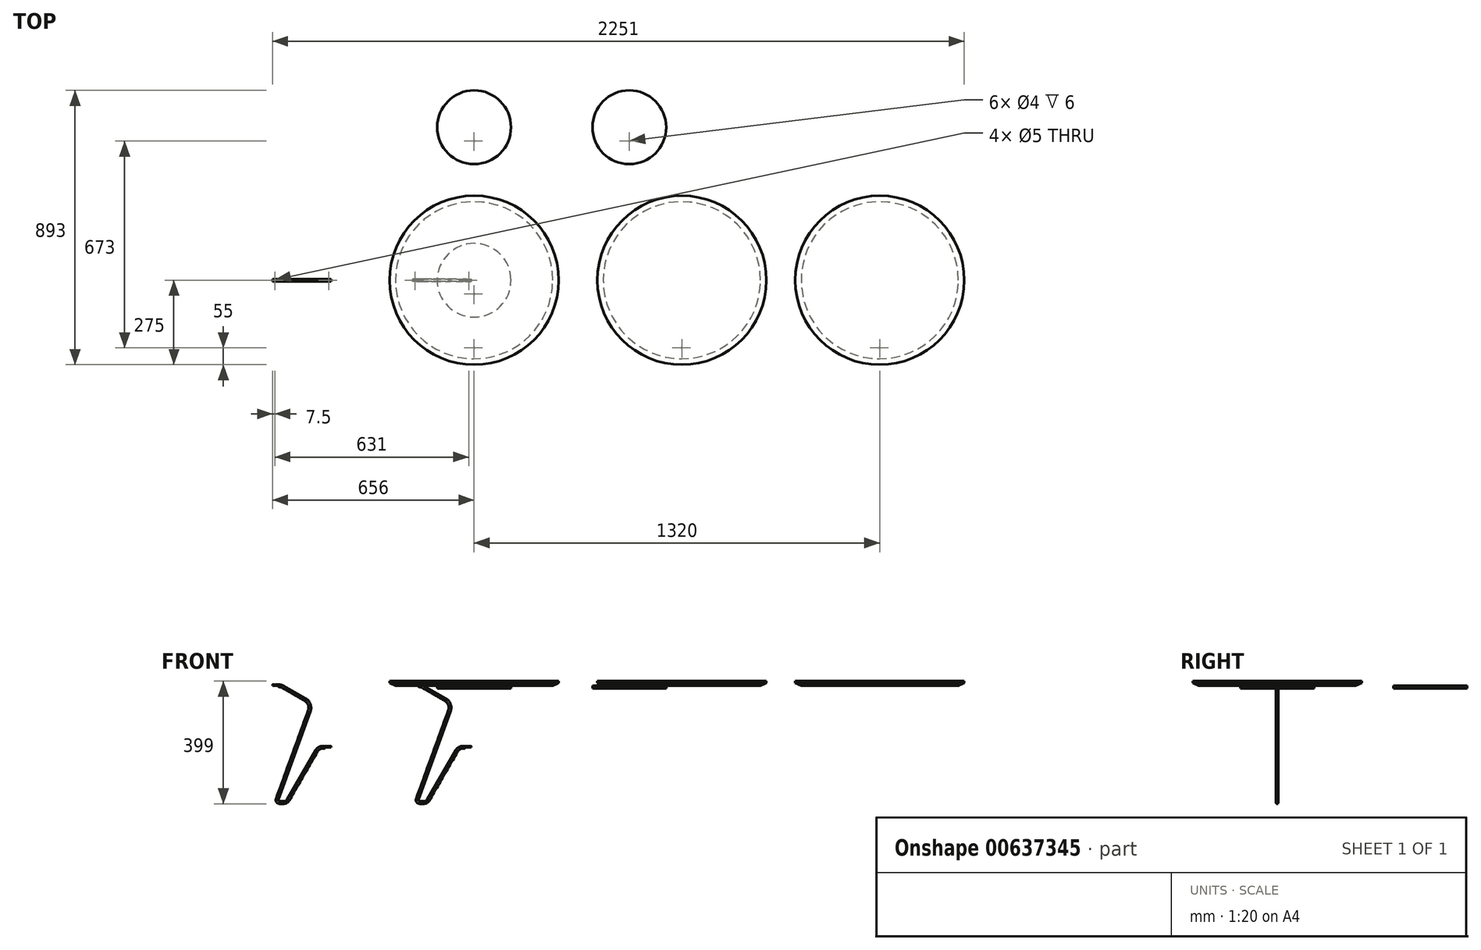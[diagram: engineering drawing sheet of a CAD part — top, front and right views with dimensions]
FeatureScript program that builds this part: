
annotation { "Feature Type Name" : "Feature", "Feature Type Description" : "" }
export const myFeature = defineFeature(function(context is Context, id is Id, definition is map)
    precondition{}
    {
        {
            var Q0;
            Q0=qCreatedBy(makeId("Front.planeOp"),FACE);
            var sketch = newSketch(context, id + "F0", { "sketchPlane" : qUnion([Q0])});
            skLineSegment(sketch, "E0", {"start": v(-200, 0) * mm, "end": v(-180, 0) * mm});
            skLineSegment(sketch, "E1", {"start": v(-165, -4.02) * mm, "end": v(-93.49, -45.3) * mm});
            skLineSegment(sketch, "E2", {"start": v(-80.3, -81.55) * mm, "end": v(-185.02, -369.26) * mm});
            skLineSegment(sketch, "E3", {"start": v(-177.5, -380) * mm, "end": v(-163.16, -380) * mm});
            skLineSegment(sketch, "E4", {"start": v(-149.3, -372) * mm, "end": v(-57.22, -212.5) * mm});
            skLineSegment(sketch, "E5", {"start": v(-35.57, -200) * mm, "end": v(0, -200) * mm});
            skPoint(sketch, "E6.visualSharp", {"position": v(-71.69, -57.9) * mm});
            skArc(sketch, "E6.filletArc", {"start": v(-80.3, -81.55) * mm, "mid": v(-80.3, -61.03) * mm, "end": v(-93.49, -45.3) * mm});
            skPoint(sketch, "E7.visualSharp", {"position": v(-50, -200) * mm});
            skArc(sketch, "E7.filletArc", {"start": v(-35.57, -200) * mm, "mid": v(-48.07, -203.35) * mm, "end": v(-57.22, -212.5) * mm});
            skPoint(sketch, "E8.visualSharp", {"position": v(-153.92, -380) * mm});
            skArc(sketch, "E8.filletArc", {"start": v(-163.16, -380) * mm, "mid": v(-155.16, -377.86) * mm, "end": v(-149.3, -372) * mm});
            skPoint(sketch, "E9.visualSharp", {"position": v(-188.92, -380) * mm});
            skArc(sketch, "E9.filletArc", {"start": v(-185.02, -369.26) * mm, "mid": v(-184.05, -376.59) * mm, "end": v(-177.5, -380) * mm});
            skPoint(sketch, "E10.visualSharp", {"position": v(-171.96, 0) * mm});
            skArc(sketch, "E10.filletArc", {"start": v(-165, -4.02) * mm, "mid": v(-172.24, -1.02) * mm, "end": v(-180, 0) * mm});
            skSolve(sketch);
        }
        {
            var Q0;
            Q0=qCreatedBy(makeId("Right.planeOp"),FACE);
            var sketch = newSketch(context, id + "F1", { "sketchPlane" : qUnion([Q0])});
            skCircle(sketch, "E11", {"center": v(0, -200) * mm, "radius": 4 * mm});
            skSolve(sketch);
        }
        {
            var Q0;
            Q0=makeQuery(id+"F1.imprint","IMPRINT",FACE,{"disambiguationData":[TD([[makeQuery(id+"F1.imprint","IMPRINT",EDGE,{"derivedFrom":sQuery(id+"F1.wireOp",EDGE,"E11")}),1.0]])]});
            var Q1;
            Q1=sQuery(id+"F0.wireOp",EDGE,"E5");
            var Q2;
            Q2=sQuery(id+"F0.wireOp",EDGE,"E7.filletArc");
            var Q3;
            Q3=sQuery(id+"F0.wireOp",EDGE,"E4");
            var Q4;
            Q4=sQuery(id+"F0.wireOp",EDGE,"E8.filletArc");
            var Q5;
            Q5=sQuery(id+"F0.wireOp",EDGE,"E3");
            var Q6;
            Q6=sQuery(id+"F0.wireOp",EDGE,"E9.filletArc");
            var Q7;
            Q7=sQuery(id+"F0.wireOp",EDGE,"E2");
            var Q8;
            Q8=sQuery(id+"F0.wireOp",EDGE,"E6.filletArc");
            var Q9;
            Q9=sQuery(id+"F0.wireOp",EDGE,"E1");
            var Q10;
            Q10=sQuery(id+"F0.wireOp",EDGE,"E10.filletArc");
            var Q11;
            Q11=sQuery(id+"F0.wireOp",EDGE,"E0");
            sweep(context, id + "F2", {"profiles" : qUnion([Q0]), "path" : qUnion([Q1, Q2, Q3, Q4, Q5, Q6, Q7, Q8, Q9, Q10, Q11])});
        }
        {
            var Q0;
            Q0=makeQuery(id+"F2.opSweep","CAP_FACE",FACE,{"disambiguationData":[OSD([sQuery(id+"F0.wireOp",VERTEX,"E0.start"),sQuery(id+"F1.wireOp",EDGE,"E11")])],"isStart":false});
            var sketch = newSketch(context, id + "F3", { "sketchPlane" : qUnion([Q0])});
            skLineSegment(sketch, "E12", {"start": v(4, 0) * mm, "end": v(-4, 0) * mm});
            skArc(sketch, "E13", {"start": v(-4, 0) * mm, "mid": v(0, -4) * mm, "end": v(4, 0) * mm});
            skSolve(sketch);
        }
        {
            var Q0;
            Q0 = qSketchRegion(id + "F3", true);
            extrude(context, id + "F4", {"entities" : qUnion([Q0]), "operationType" : NewBodyOperationType.REMOVE, "oppositeDirection" : true, "depth" : 20 * mm, "offsetDistance" : 25 * mm});
        }
        {
            var Q0;
            Q0=makeQuery(id+"F4.boolean.opBoolean","COPY",FACE,{"derivedFrom":makeQuery(id+"F4.opExtrude","SWEPT_FACE",FACE,{"disambiguationData":[OSD([sQuery(id+"F3.wireOp",EDGE,"E12")])]})});
            var sketch = newSketch(context, id + "F5", { "sketchPlane" : qUnion([Q0])});
            skCircle(sketch, "E14", {"center": v(-192.5, 0) * mm, "radius": 2.5 * mm});
            skPoint(sketch, "E14.centerSnap0", {"position": v(-200, 0) * mm});
            skSolve(sketch);
        }
        {
            var Q0;
            Q0 = qSketchRegion(id + "F5", true);
            extrude(context, id + "F6", {"entities" : qUnion([Q0]), "operationType" : NewBodyOperationType.REMOVE, "endBound" : BoundingType.THROUGH_ALL, "oppositeDirection" : true, "depth" : 25 * mm, "offsetDistance" : 25 * mm});
        }
        {
            var Q0;
            Q0=makeQuery(id+"F2.opSweep","CAP_FACE",FACE,{"disambiguationData":[OSD([sQuery(id+"F0.wireOp",VERTEX,"E5.end"),sQuery(id+"F1.wireOp",EDGE,"E11")])],"isStart":true});
            extrude(context, id + "F7", {"entities" : qUnion([Q0]), "operationType" : NewBodyOperationType.REMOVE, "oppositeDirection" : true, "depth" : 10 * mm, "offsetDistance" : 25 * mm});
        }
        {
            var Q0;
            Q0=makeQuery(id+"F7.boolean.opBoolean","COPY",FACE,{"derivedFrom":makeQuery(id+"F7.opExtrude","CAP_FACE",FACE,{"disambiguationData":[OSD([sQuery(id+"F0.wireOp",VERTEX,"E5.end"),sQuery(id+"F1.wireOp",EDGE,"E11")])],"isStart":false})});
            var sketch = newSketch(context, id + "F8", { "sketchPlane" : qUnion([Q0])});
            skLineSegment(sketch, "E15", {"start": v(-4, -200) * mm, "end": v(4, -200) * mm});
            skPoint(sketch, "E16", {"position": v(0, -200) * mm});
            skArc(sketch, "E17", {"start": v(-4, -200) * mm, "mid": v(0, -204) * mm, "end": v(4, -200) * mm});
            skSolve(sketch);
        }
        {
            var Q0;
            Q0 = qSketchRegion(id + "F8", true);
            extrude(context, id + "F9", {"entities" : qUnion([Q0]), "operationType" : NewBodyOperationType.REMOVE, "oppositeDirection" : true, "depth" : 20 * mm, "offsetDistance" : 25 * mm});
        }
        {
            var Q0;
            Q0=makeQuery(id+"F9.boolean.opBoolean","COPY",FACE,{"derivedFrom":makeQuery(id+"F9.opExtrude","SWEPT_FACE",FACE,{"disambiguationData":[OSD([sQuery(id+"F8.wireOp",EDGE,"E15")])]})});
            var sketch = newSketch(context, id + "F10", { "sketchPlane" : qUnion([Q0])});
            skCircle(sketch, "E18", {"center": v(-17.5, 0) * mm, "radius": 2.5 * mm});
            skPoint(sketch, "E18.centerSnap0", {"position": v(-10, 0) * mm});
            skSolve(sketch);
        }
        {
            var Q0;
            Q0 = qSketchRegion(id + "F10", true);
            extrude(context, id + "F11", {"entities" : qUnion([Q0]), "operationType" : NewBodyOperationType.REMOVE, "endBound" : BoundingType.THROUGH_ALL, "oppositeDirection" : true, "depth" : 25 * mm, "offsetDistance" : 25 * mm});
        }
        {
            var Q0;
            Q0=makeQuery(id+"F4.boolean.opBoolean","COPY",EDGE,{"derivedFrom":makeQuery(id+"F4.opExtrude","CAP_EDGE",EDGE,{"disambiguationData":[OSD([sQuery(id+"F3.wireOp",EDGE,"E12")])],"isStart":false})});
            var Q1;
            Q1=makeQuery(id+"F9.boolean.opBoolean","COPY",EDGE,{"derivedFrom":makeQuery(id+"F9.opExtrude","CAP_EDGE",EDGE,{"disambiguationData":[OSD([sQuery(id+"F8.wireOp",EDGE,"E15")])],"isStart":false})});
            fillet(context, id + "F12", {"entities" : qUnion([Q0, Q1]), "radius" : 5 * mm, "tangentPropagation" : true, "allowEdgeOverflow" : false});
        }
        {
            var Q0;
            Q0=qCreatedBy(makeId("Top.planeOp"),FACE);
            var sketch = newSketch(context, id + "F13", { "sketchPlane" : qUnion([Q0])});
            skCircle(sketch, "E19", {"center": v(0, 0) * mm, "radius": 275 * mm});
            skSolve(sketch);
        }
        {
            var Q0;
            Q0 = qSketchRegion(id + "F13", true);
            extrude(context, id + "F14", {"entities" : qUnion([Q0]), "depth" : 15 * mm, "offsetDistance" : 25 * mm});
        }
        {
            var Q0;
            Q0=qCreatedBy(makeId("Top.planeOp"),FACE);
            var sketch = newSketch(context, id + "F15", { "sketchPlane" : qUnion([Q0])});
            skCircle(sketch, "E20", {"center": v(0, 0) * mm, "radius": 120 * mm});
            skSolve(sketch);
        }
        {
            var Q0;
            Q0=makeQuery(id+"F15.imprint","IMPRINT",FACE,{"disambiguationData":[TD([[makeQuery(id+"F15.imprint","IMPRINT",EDGE,{"derivedFrom":sQuery(id+"F15.wireOp",EDGE,"E20")}),1.0]])]});
            var Q1;
            Q1=sQuery(id+"F15.wireOp",EDGE,"E20");
            extrude(context, id + "F16", {"entities" : qUnion([Q0]), "surfaceEntities" : qUnion([Q1]), "oppositeDirection" : true, "depth" : 9 * mm, "offsetDistance" : 25 * mm});
        }
        {
            var Q0;
            Q0=makeQuery(id+"F14.opExtrude","CAP_EDGE",EDGE,{"disambiguationData":[OSD([sQuery(id+"F13.wireOp",EDGE,"E19")])],"isStart":true});
            chamfer(context, id + "F17", {"entities" : qUnion([Q0]), "chamferType" : ChamferType.OFFSET_ANGLE, "width" : 9 * mm, "oppositeDirection" : false, "angle" : 65 * degree, "tangentPropagation" : true});
        }
        {
            var Q0;
            Q0=qCreatedBy(makeId("Front.planeOp"),FACE);
            var sketch = newSketch(context, id + "F18", { "sketchPlane" : qUnion([Q0])});
            skLineSegment(sketch, "E21", {"start": v(0, 0) * mm, "end": v(0, -50) * mm, "construction": true});
            skSolve(sketch);
        }
        {
            var Q0;
            Q0=makeQuery(id+"F16.opExtrude","CAP_FACE",FACE,{"disambiguationData":[OSD([sQuery(id+"F15.wireOp",EDGE,"E20")])],"isStart":false});
            var sketch = newSketch(context, id + "F19", { "sketchPlane" : qUnion([Q0])});
            skCircle(sketch, "E22", {"center": v(0, 45) * mm, "radius": 2 * mm});
            skCircle(sketch, "E23", {"center": v(0, 0) * mm, "radius": 45 * mm, "construction": true});
            skSolve(sketch);
        }
        {
            var Q0;
            Q0=makeQuery(id+"F19.imprint","IMPRINT",FACE,{"disambiguationData":[TD([[makeQuery(id+"F19.imprint","IMPRINT",EDGE,{"derivedFrom":sQuery(id+"F19.wireOp",EDGE,"E22")}),1.0]])]});
            var Q1;
            Q1=sQuery(id+"F19.wireOp",EDGE,"E22");
            extrude(context, id + "F20", {"entities" : qUnion([Q0]), "operationType" : NewBodyOperationType.REMOVE, "surfaceEntities" : qUnion([Q1]), "oppositeDirection" : true, "depth" : 6 * mm, "offsetDistance" : 25 * mm});
        }
        {
            var Q0;
            Q0=makeQuery(id+"F14.opExtrude","CAP_FACE",FACE,{"disambiguationData":[OSD([sQuery(id+"F13.wireOp",EDGE,"E19")])],"isStart":true});
            var sketch = newSketch(context, id + "F21", { "sketchPlane" : qUnion([Q0])});
            skCircle(sketch, "E24", {"center": v(0, 0) * mm, "radius": 220 * mm, "construction": true});
            skCircle(sketch, "E25", {"center": v(0, 220) * mm, "radius": 2 * mm});
            skSolve(sketch);
        }
        {
            var Q0;
            Q0 = qSketchRegion(id + "F21", true);
            extrude(context, id + "F22", {"entities" : qUnion([Q0]), "operationType" : NewBodyOperationType.REMOVE, "oppositeDirection" : true, "depth" : 6 * mm, "offsetDistance" : 25 * mm});
        }
        {
            var Q0;
            Q0=makeQuery(id+"F16.opExtrude","SWEPT_BODY",BODY,{"disambiguationData":[OSD([sQuery(id+"F15.wireOp",EDGE,"E20")])]});
            transform(context, id + "F23", {"entities" : qUnion([Q0]), "transformType" : TransformType.TRANSLATION_3D, "dx" : 0 * mm, "dy" : 498 * mm, "dz" : 0 * mm, "makeCopy" : true});
        }
        {
            var Q0;
            Q0=makeQuery(id+"F14.opExtrude","SWEPT_BODY",BODY,{"disambiguationData":[OSD([sQuery(id+"F13.wireOp",EDGE,"E19")])]});
            transform(context, id + "F24", {"entities" : qUnion([Q0]), "transformType" : TransformType.TRANSLATION_3D, "dx" : 1320 * mm, "dy" : 0 * mm, "dz" : 0 * mm, "makeCopy" : true});
        }
        {
            var Q0;
            Q0=makeQuery(id+"F23.opPattern","COPY",BODY,{"derivedFrom":makeQuery(id+"F16.opExtrude","SWEPT_BODY",BODY,{"disambiguationData":[OSD([sQuery(id+"F15.wireOp",EDGE,"E20")])]}),"instanceName":"1"});
            transform(context, id + "F25", {"entities" : qUnion([Q0]), "transformType" : TransformType.TRANSLATION_3D, "dx" : 505 * mm, "dy" : 0 * mm, "dz" : 0 * mm, "makeCopy" : true});
        }
        {
            var Q0;
            Q0=makeQuery(id+"F14.opExtrude","SWEPT_BODY",BODY,{"disambiguationData":[OSD([sQuery(id+"F13.wireOp",EDGE,"E19")])]});
            transform(context, id + "F26", {"entities" : qUnion([Q0]), "transformType" : TransformType.TRANSLATION_3D, "dx" : 676 * mm, "dy" : 0 * mm, "dz" : 0 * mm, "makeCopy" : true});
        }
        {
            var Q0;
            Q0=makeQuery(id+"F2.opSweep","SWEPT_BODY",BODY,{"disambiguationData":[OSD([sQuery(id+"F0.wireOp",EDGE,"E0"),sQuery(id+"F1.wireOp",EDGE,"E11")])]});
            transform(context, id + "F27", {"entities" : qUnion([Q0]), "transformType" : TransformType.TRANSLATION_3D, "dx" : -456 * mm, "dy" : 0 * mm, "dz" : 0 * mm, "makeCopy" : true});
        }
    });
